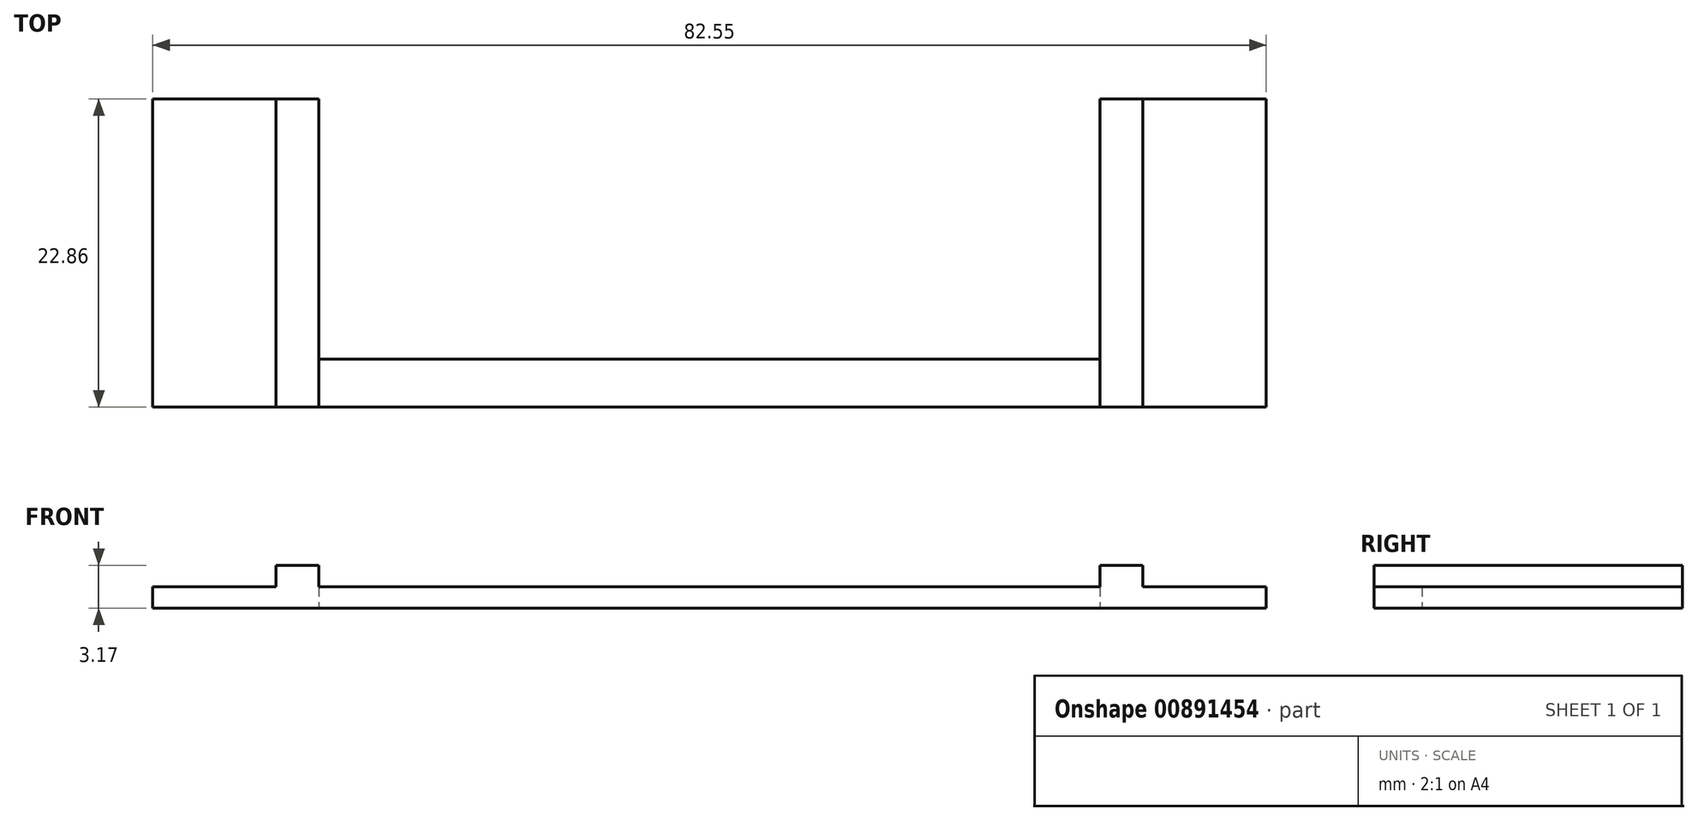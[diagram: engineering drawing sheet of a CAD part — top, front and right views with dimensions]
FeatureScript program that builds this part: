
annotation { "Feature Type Name" : "Feature", "Feature Type Description" : "" }
export const myFeature = defineFeature(function(context is Context, id is Id, definition is map)
    precondition{}
    {
        {
            var Q0;
            Q0=qCreatedBy(makeId("Top.planeOp"),FACE);
            var sketch = newSketch(context, id + "F0", { "sketchPlane" : qUnion([Q0])});
            skLineSegment(sketch, "E0.bottom", {"start": v(0, 0) * mm, "end": v(12.32, 0) * mm});
            skLineSegment(sketch, "E0.top", {"start": v(0, 22.86) * mm, "end": v(12.32, 22.86) * mm});
            skLineSegment(sketch, "E0.left", {"start": v(0, 0) * mm, "end": v(0, 22.86) * mm});
            skLineSegment(sketch, "E0.right", {"start": v(12.32, 3.56) * mm, "end": v(12.32, 22.86) * mm});
            skLineSegment(sketch, "E1.bottom", {"start": v(12.32, 0) * mm, "end": v(70.23, 0) * mm});
            skLineSegment(sketch, "E1.top", {"start": v(12.32, 3.56) * mm, "end": v(70.23, 3.56) * mm});
            skLineSegment(sketch, "E2.bottom", {"start": v(70.23, 0) * mm, "end": v(82.55, 0) * mm});
            skLineSegment(sketch, "E2.top", {"start": v(70.23, 22.86) * mm, "end": v(82.55, 22.86) * mm});
            skLineSegment(sketch, "E2.left", {"start": v(70.23, 3.56) * mm, "end": v(70.23, 22.86) * mm});
            skLineSegment(sketch, "E2.right", {"start": v(82.55, 0) * mm, "end": v(82.55, 22.86) * mm});
            skSolve(sketch);
        }
        {
            var Q0;
            Q0=makeQuery(id+"F0.imprint","IMPRINT",FACE,{"disambiguationData":[TD([[makeQuery(id+"F0.imprint","IMPRINT",EDGE,{"derivedFrom":sQuery(id+"F0.wireOp",EDGE,"E0.bottom")}),1.0]])]});
            extrude(context, id + "F1", {"entities" : qUnion([Q0]), "depth" : 1.59 * mm, "offsetDistance" : 25.4 * mm});
        }
        {
            var Q0;
            Q0=makeQuery(id+"F1.opExtrude","CAP_FACE",FACE,{"disambiguationData":[OSD([sQuery(id+"F0.wireOp",EDGE,"E0.bottom"),sQuery(id+"F0.wireOp",EDGE,"E0.top"),sQuery(id+"F0.wireOp",EDGE,"E0.left"),sQuery(id+"F0.wireOp",EDGE,"E0.right"),sQuery(id+"F0.wireOp",EDGE,"E1.bottom"),sQuery(id+"F0.wireOp",EDGE,"E1.top"),sQuery(id+"F0.wireOp",EDGE,"E2.bottom"),sQuery(id+"F0.wireOp",EDGE,"E2.top"),sQuery(id+"F0.wireOp",EDGE,"E2.left"),sQuery(id+"F0.wireOp",EDGE,"E2.right")])],"isStart":false});
            var sketch = newSketch(context, id + "F2", { "sketchPlane" : qUnion([Q0])});
            skLineSegment(sketch, "E3.bottom", {"start": v(12.32, 22.86) * mm, "end": v(9.14, 22.86) * mm});
            skLineSegment(sketch, "E3.top", {"start": v(12.32, 0) * mm, "end": v(9.14, 0) * mm});
            skLineSegment(sketch, "E3.left", {"start": v(12.32, 22.86) * mm, "end": v(12.32, 0) * mm});
            skLineSegment(sketch, "E3.right", {"start": v(9.14, 22.86) * mm, "end": v(9.14, 0) * mm});
            skLineSegment(sketch, "E4.bottom", {"start": v(70.23, 22.86) * mm, "end": v(73.4, 22.86) * mm});
            skLineSegment(sketch, "E4.top", {"start": v(70.23, 0) * mm, "end": v(73.4, 0) * mm});
            skLineSegment(sketch, "E4.left", {"start": v(70.23, 22.86) * mm, "end": v(70.23, 0) * mm});
            skLineSegment(sketch, "E4.right", {"start": v(73.4, 22.86) * mm, "end": v(73.4, 0) * mm});
            skSolve(sketch);
        }
        {
            var Q0;
            {var subQ3=sQuery(id+"F2.wireOp",EDGE,"E3.bottom");Q0=makeQuery(id+"F2.imprint","IMPRINT",FACE,{"disambiguationData":[TD([[makeQuery(id+"F2.imprint","IMPRINT",EDGE,{"derivedFrom":subQ3}),-1.0]])]});}
            var Q1;
            {var subQ3=sQuery(id+"F2.wireOp",EDGE,"E4.bottom");Q1=makeQuery(id+"F2.imprint","IMPRINT",FACE,{"disambiguationData":[TD([[makeQuery(id+"F2.imprint","IMPRINT",EDGE,{"derivedFrom":subQ3}),-1.0]])]});}
            extrude(context, id + "F3", {"entities" : qUnion([Q0, Q1]), "operationType" : NewBodyOperationType.ADD, "depth" : 1.59 * mm, "offsetDistance" : 25.4 * mm});
        }
    });
